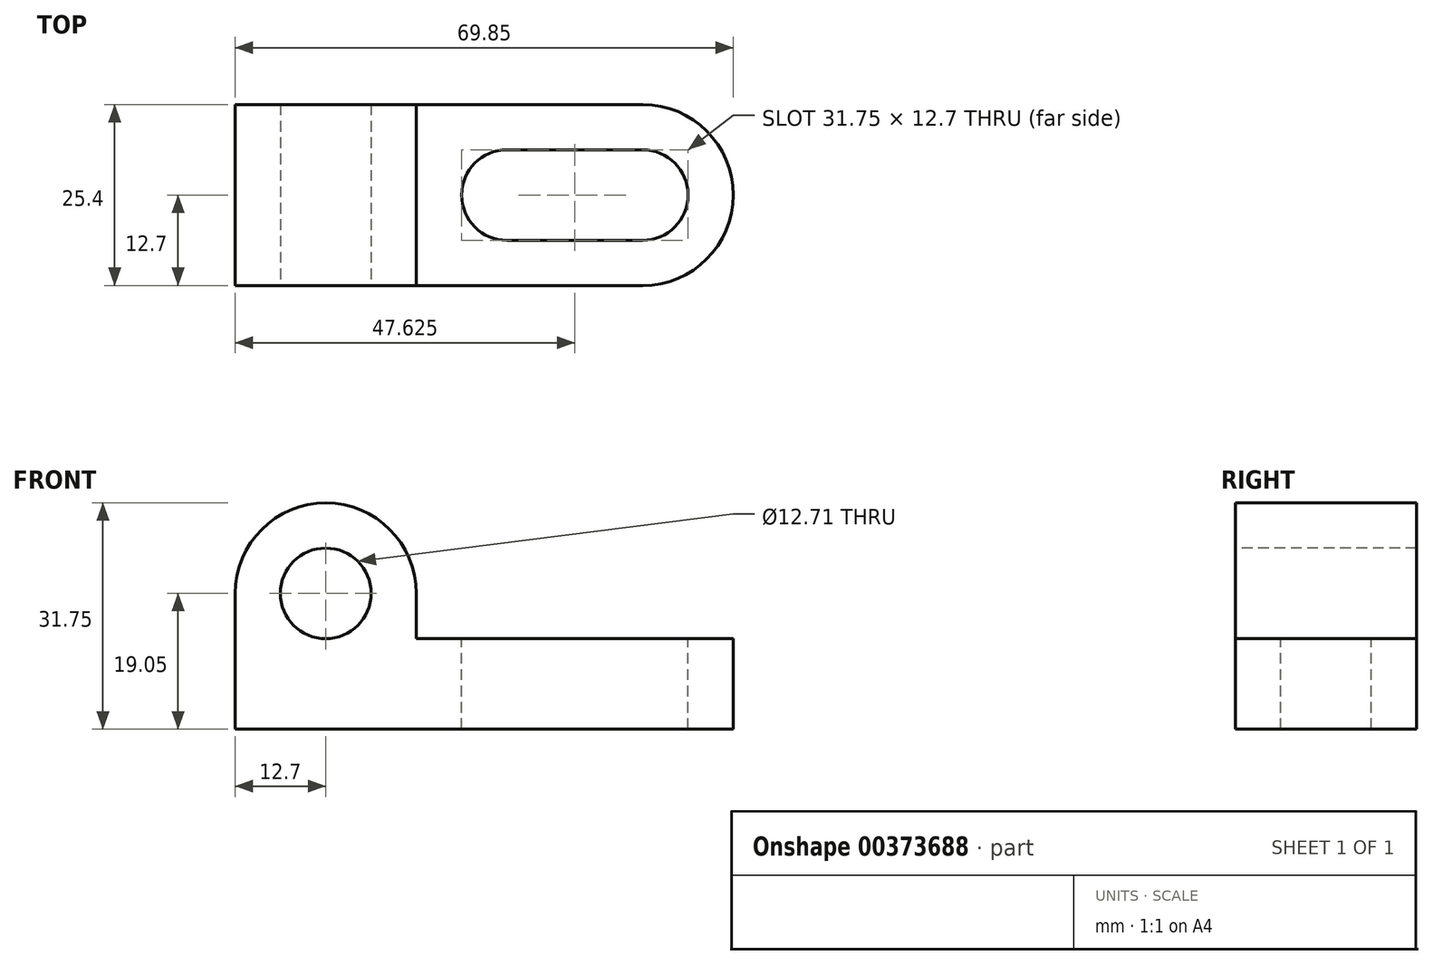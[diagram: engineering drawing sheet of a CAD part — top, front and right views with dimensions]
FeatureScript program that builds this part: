
annotation { "Feature Type Name" : "Feature", "Feature Type Description" : "" }
export const myFeature = defineFeature(function(context is Context, id is Id, definition is map)
    precondition{}
    {
        {
            var Q0;
            Q0=qCreatedBy(makeId("Front.planeOp"),FACE);
            var sketch = newSketch(context, id + "F0", { "sketchPlane" : qUnion([Q0])});
            skLineSegment(sketch, "E0", {"start": v(0, 0) * mm, "end": v(69.85, 0) * mm});
            skLineSegment(sketch, "E1", {"start": v(69.85, 0) * mm, "end": v(69.85, 12.7) * mm});
            skLineSegment(sketch, "E2", {"start": v(69.85, 12.7) * mm, "end": v(25.4, 12.7) * mm});
            skLineSegment(sketch, "E3", {"start": v(25.4, 12.7) * mm, "end": v(25.4, 31.75) * mm});
            skLineSegment(sketch, "E4", {"start": v(25.4, 31.75) * mm, "end": v(0, 31.75) * mm});
            skLineSegment(sketch, "E5", {"start": v(0, 31.75) * mm, "end": v(0, 0) * mm});
            skSolve(sketch);
        }
        {
            var Q0;
            Q0 = qSketchRegion(id + "F0", true);
            extrude(context, id + "F1", {"entities" : qUnion([Q0]), "depth" : 25.4 * mm});
        }
        {
            var Q0;
            Q0=makeQuery(id+"F1.opExtrude","CAP_FACE",FACE,{"disambiguationData":[OSD([sQuery(id+"F0.wireOp",EDGE,"E0"),sQuery(id+"F0.wireOp",EDGE,"E1"),sQuery(id+"F0.wireOp",EDGE,"E2"),sQuery(id+"F0.wireOp",EDGE,"E3"),sQuery(id+"F0.wireOp",EDGE,"E4"),sQuery(id+"F0.wireOp",EDGE,"E5")])],"isStart":false});
            var sketch = newSketch(context, id + "F2", { "sketchPlane" : qUnion([Q0])});
            skCircle(sketch, "E6", {"center": v(12.7, 19.05) * mm, "radius": 6.35 * mm});
            skPoint(sketch, "E7.endSnap0", {"position": v(25.4, 22.22) * mm});
            skArc(sketch, "E8", {"start": v(25.4, 19.05) * mm, "mid": v(12.7, 31.75) * mm, "end": v(0, 19.05) * mm});
            skSolve(sketch);
        }
        {
            var Q0;
            {var subQ0=sQuery(id+"F2.wireOp",EDGE,"E8");var subQ1=makeQuery(id+"F1.opExtrude","CAP_EDGE",EDGE,{"disambiguationData":[OSD([sQuery(id+"F0.wireOp",EDGE,"E3")])],"isStart":false});var subQ2=makeQuery(id+"F2.imprint","INTERSECT",VERTEX,{"derivedFrom":[subQ1,subQ0]});Q0=makeQuery(id+"F2.imprint","IMPRINT",FACE,{"disambiguationData":[TD([[makeQuery(id+"F2.imprint","IMPRINT",EDGE,{"disambiguationData":[TD([[subQ2,-1.0]])],"derivedFrom":subQ0}),-1.0]])]});}
            var Q1;
            {var subQ0=sQuery(id+"F2.wireOp",EDGE,"E8");var subQ1=makeQuery(id+"F1.opExtrude","CAP_EDGE",EDGE,{"disambiguationData":[OSD([sQuery(id+"F0.wireOp",EDGE,"E5")])],"isStart":false});var subQ2=makeQuery(id+"F2.imprint","INTERSECT",VERTEX,{"derivedFrom":[subQ1,subQ0]});Q1=makeQuery(id+"F2.imprint","IMPRINT",FACE,{"disambiguationData":[TD([[makeQuery(id+"F2.imprint","IMPRINT",EDGE,{"disambiguationData":[TD([[subQ2,1.0]])],"derivedFrom":subQ0}),-1.0]])]});}
            var Q2;
            Q2=makeQuery(id+"F2.imprint","IMPRINT",FACE,{"disambiguationData":[TD([[makeQuery(id+"F2.imprint","IMPRINT",EDGE,{"derivedFrom":sQuery(id+"F2.wireOp",EDGE,"E6")}),1.0]])]});
            extrude(context, id + "F3", {"entities" : qUnion([Q0, Q1, Q2]), "operationType" : NewBodyOperationType.REMOVE, "oppositeDirection" : true, "depth" : 25.4 * mm});
        }
        {
            var Q0;
            Q0=makeQuery(id+"F1.opExtrude","SWEPT_FACE",FACE,{"disambiguationData":[OSD([sQuery(id+"F0.wireOp",EDGE,"E2")])]});
            var sketch = newSketch(context, id + "F4", { "sketchPlane" : qUnion([Q0])});
            skArc(sketch, "E9", {"start": v(57.15, -25.4) * mm, "mid": v(69.85, -12.7) * mm, "end": v(57.15, 0) * mm});
            skCircle(sketch, "E10", {"center": v(38.1, -12.7) * mm, "radius": 6.35 * mm});
            skCircle(sketch, "E11", {"center": v(57.15, -12.7) * mm, "radius": 6.35 * mm});
            skLineSegment(sketch, "E12", {"start": v(38.1, -19.05) * mm, "end": v(57.15, -19.05) * mm});
            skLineSegment(sketch, "E13", {"start": v(38.1, -6.35) * mm, "end": v(57.15, -6.35) * mm});
            skSolve(sketch);
        }
        {
            var Q0;
            {var subQ0=sQuery(id+"F4.wireOp",EDGE,"E10");var subQ1=makeQuery(id+"F4.imprint","INTERSECT",VERTEX,{"derivedFrom":[subQ0,sQuery(id+"F4.wireOp",EDGE,"E12")]});Q0=makeQuery(id+"F4.imprint","IMPRINT",FACE,{"disambiguationData":[TD([[makeQuery(id+"F4.imprint","IMPRINT",EDGE,{"disambiguationData":[TD([[subQ1,1.0]])],"derivedFrom":subQ0}),1.0]])]});}
            var Q1;
            {var subQ0=sQuery(id+"F4.wireOp",EDGE,"E12");Q1=makeQuery(id+"F4.imprint","IMPRINT",FACE,{"disambiguationData":[TD([[makeQuery(id+"F4.imprint","IMPRINT",EDGE,{"derivedFrom":subQ0}),1.0]])]});}
            var Q2;
            {var subQ0=sQuery(id+"F4.wireOp",EDGE,"E11");var subQ1=makeQuery(id+"F4.imprint","INTERSECT",VERTEX,{"derivedFrom":[subQ0,sQuery(id+"F4.wireOp",EDGE,"E12")]});Q2=makeQuery(id+"F4.imprint","IMPRINT",FACE,{"disambiguationData":[TD([[makeQuery(id+"F4.imprint","IMPRINT",EDGE,{"disambiguationData":[TD([[subQ1,1.0]])],"derivedFrom":subQ0}),1.0]])]});}
            var Q3;
            {var subQ0=sQuery(id+"F4.wireOp",EDGE,"E9");var subQ1=sQuery(id+"F0.wireOp",EDGE,"E2");var subQ2=makeQuery(id+"F1.opExtrude","CAP_EDGE",EDGE,{"disambiguationData":[OSD([subQ1])],"isStart":true});var subQ3=makeQuery(id+"F4.imprint","INTERSECT",VERTEX,{"derivedFrom":[subQ2,subQ0]});Q3=makeQuery(id+"F4.imprint","IMPRINT",FACE,{"disambiguationData":[TD([[makeQuery(id+"F4.imprint","IMPRINT",EDGE,{"disambiguationData":[TD([[subQ3,1.0]])],"derivedFrom":subQ0}),-1.0]])]});}
            var Q4;
            {var subQ0=sQuery(id+"F4.wireOp",EDGE,"E9");var subQ1=sQuery(id+"F0.wireOp",EDGE,"E2");var subQ2=makeQuery(id+"F1.opExtrude","CAP_EDGE",EDGE,{"disambiguationData":[OSD([subQ1])],"isStart":false});var subQ3=makeQuery(id+"F4.imprint","INTERSECT",VERTEX,{"derivedFrom":[subQ2,subQ0]});Q4=makeQuery(id+"F4.imprint","IMPRINT",FACE,{"disambiguationData":[TD([[makeQuery(id+"F4.imprint","IMPRINT",EDGE,{"disambiguationData":[TD([[subQ3,-1.0]])],"derivedFrom":subQ0}),-1.0]])]});}
            extrude(context, id + "F5", {"entities" : qUnion([Q0, Q1, Q2, Q3, Q4]), "operationType" : NewBodyOperationType.REMOVE, "oppositeDirection" : true, "depth" : 25.4 * mm});
        }
    });
